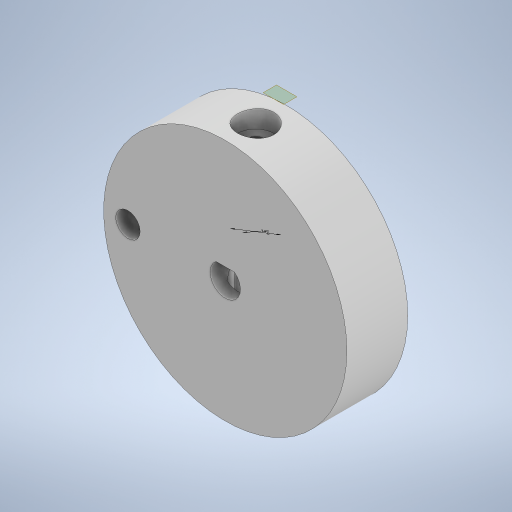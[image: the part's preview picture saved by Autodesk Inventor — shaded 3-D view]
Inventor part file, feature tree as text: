
AUTODESK INVENTOR PART (.ipt)
format: ipt  version: 2024 (Build 280153000, 153)  size: 269,312 bytes
history: native  units: mm
features: extrude x6, sketch x5, other x1, plane x1
ambient origin geometry x8: Origin, YZ Plane, XZ Plane, XY Plane, X Axis, Y Axis, Z Axis, Center Point
bodies: Body1 (feature_tree)
feature tree (13):
  other  "實體1"
  extrude  "擠出1"  Depth=5.0mm
  sketch  "草圖2"
  extrude  "擠出2"  Depth=4.48mm
  extrude  "擠出3"  Depth=40.0mm
  extrude  "擠出4"  Depth=10.0mm TaperAngle=0.0deg
  plane  "工作平面1"
  extrude  "擠出5"  Depth=2.5mm TaperAngle=0.0deg
  extrude  "擠出6"  TaperAngle=0.0deg  [1 undecoded]
  sketch  "草圖1"
  sketch  "草圖4"
  sketch  "草圖5"
  sketch  "草圖6"
note: 1 required parameter value undecoded (feature->parameter linkage not recoverable at this tier; creation-order binding heuristic only, values carry confidence <= 0.55)
